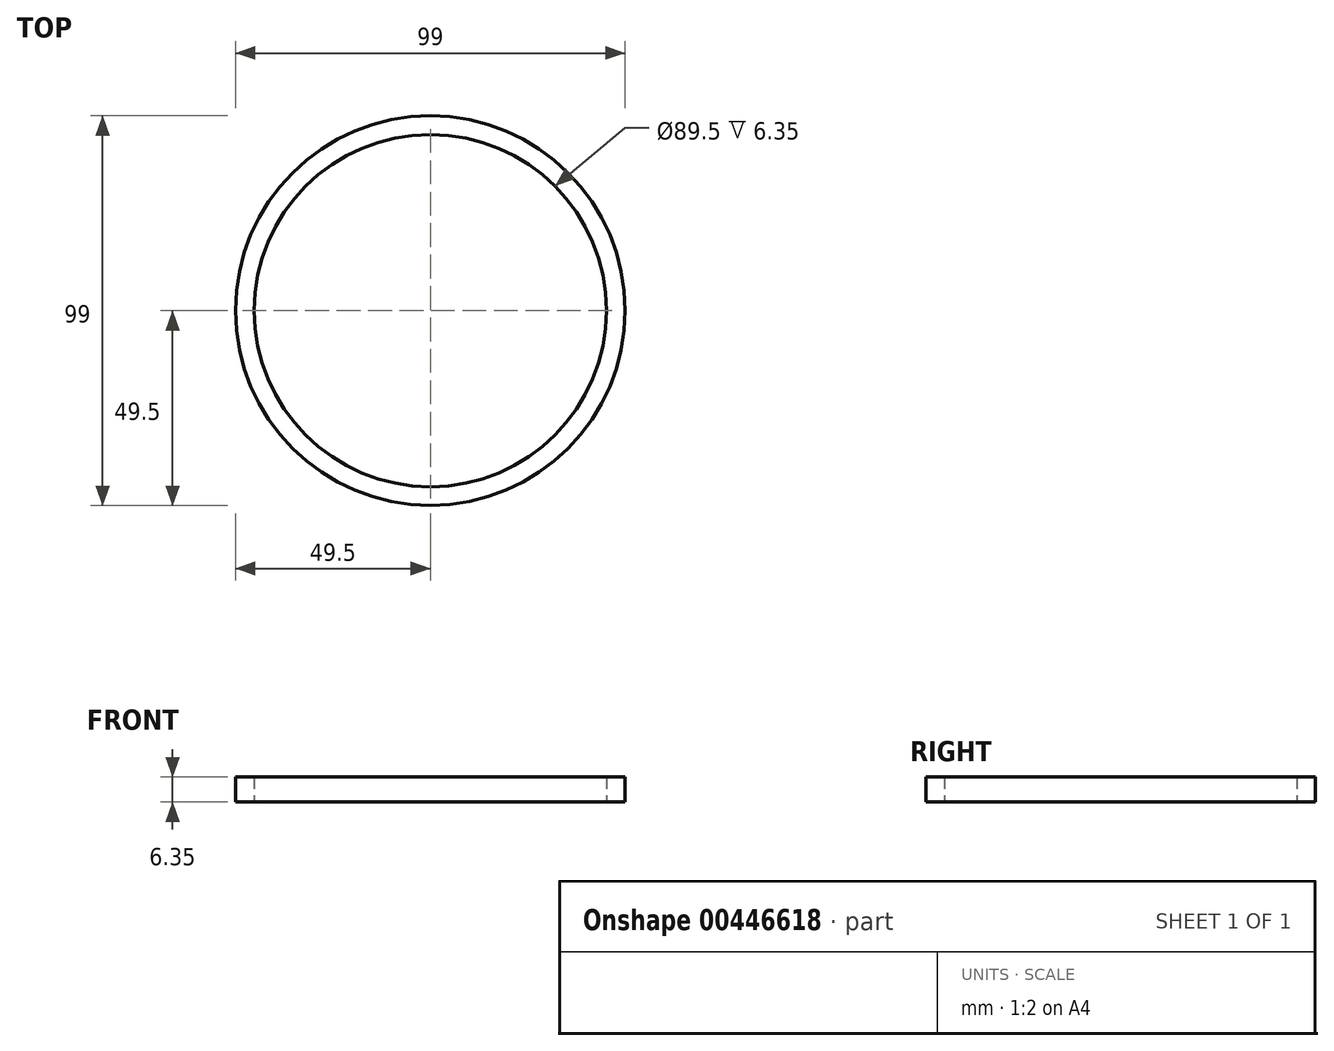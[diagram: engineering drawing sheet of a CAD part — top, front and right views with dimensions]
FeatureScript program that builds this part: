
annotation { "Feature Type Name" : "Feature", "Feature Type Description" : "" }
export const myFeature = defineFeature(function(context is Context, id is Id, definition is map)
    precondition{}
    {
        {
            var Q0;
            Q0=qCreatedBy(makeId("Top.planeOp"),FACE);
            var sketch = newSketch(context, id + "F0", { "sketchPlane" : qUnion([Q0])});
            skCircle(sketch, "E0", {"center": v(0, 0) * mm, "radius": 44.75 * mm});
            skCircle(sketch, "E1", {"center": v(0, 0) * mm, "radius": 49.5 * mm});
            skSolve(sketch);
        }
        {
            var Q0;
            Q0 = qSketchRegion(id + "F0", true);
            extrude(context, id + "F1", {"entities" : qUnion([Q0]), "depth" : 6.35 * mm});
        }
    });
